# Revit family: Камин на основе стены
name_source: partatom
category: Оборудование
units: mm (PartAtom-declared; Revit-internal decimal feet)

## family parameters
Всегда вертикально = Да
Классификация = Нет
Общий = Нет
Основа = Стена
При загрузке вырезать с полостями = Нет
Размер круглого соединителя = Использовать диаметр
Тип детали = Нормальный
Точка расчета площади = Нет

## types (12) — shared parameters
Толщина камина = 307 мм

## per-type parameters (varying)
| type | Типы | Ширина камина |
| Dimplex Vivente 75 | Камин : Dimplex Vivente 75 | 750 мм |
| Dimplex Vivente 75 установка в нишу | Камин : Dimplex Vivente 75 установка в нишу | 750 мм |
| Dimplex Vivente 75 установка слева | Камин : Dimplex Vivente 75 установка слева | 750 мм |
| Dimplex Vivente 75 установка справа | Камин : Dimplex Vivente 75 установка справа | 750 мм |
| Dimplex Vivente 100 | Камин : Dimplex Vivente 100 | 1000 мм |
| Dimplex Vivente 100 установка в нишу | Камин : Dimplex Vivente 100 установка в нишу | 1000 мм |
| Dimplex Vivente 100 установка слева | Камин : Dimplex Vivente 100 установка слева | 1000 мм |
| Dimplex Vivente 100 установка справа | Камин : Dimplex Vivente 100 установка справа | 1000 мм |
| Dimplex Vivente 150 | Камин : Dimplex Vivente 150 | 1500 мм |
| Dimplex Vivente 150 установка в нишу | Камин : Dimplex Vivente 150 установка в нишу | 1500 мм |
| Dimplex Vivente 150 установка слева | Камин : Dimplex Vivente 100 установка слева | 1500 мм |
| Dimplex Vivente 150 установка справа | Камин : Dimplex Vivente 150 установка справа | 1500 мм |
